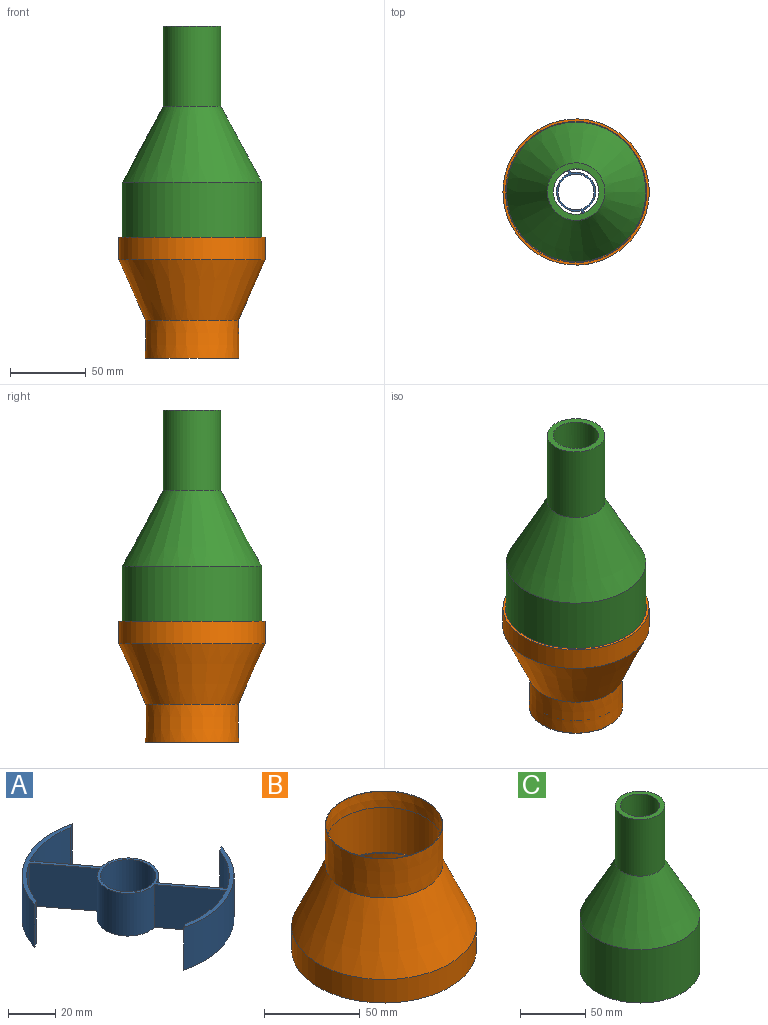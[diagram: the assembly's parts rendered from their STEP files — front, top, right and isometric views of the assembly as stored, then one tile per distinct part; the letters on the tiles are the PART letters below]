
ASSEMBLY  parts=3 mates=2
PART A: 19 faces, bbox 85.6x89.4x22 mm
  f0: cylinder r=12.95mm len=24.99mm, axis (0,0,-1), area 859.8mm2, adj f7,f10,f11,f12
  f1: plane 24.29x22mm, normal (0.8,0.6,0), area 670mm2, adj f2,f8,f10,f11
  f2: cylinder r=42.7mm len=29.3mm, axis (0,0,-1), area 668.5mm2, adj f1,f3,f10,f11
  f3: plane 22x2.6mm, normal (0.5,-0.87,0), area 66mm2, adj f2,f4,f10,f11
  f4: cylinder r=44.7mm len=53.09mm, axis (0,0,-1), area 1486.1mm2, adj f3,f5,f10,f11
  f5: plane 22x2.6mm, normal (0.5,-0.87,0), area 66mm2, adj f4,f6,f10,f11
  f6: cylinder r=42.7mm len=22mm, axis (0,0,-1), area 619.9mm2, adj f5,f7,f10,f11
  f7: plane 23.95x22mm, normal (-0.8,-0.61,0), area 661.9mm2, adj f0,f6,f10,f11
  f8: cylinder r=12.95mm len=24.99mm, axis (0,0,-1), area 859.8mm2, adj f1,f10,f11,f18
  f9: cylinder r=11.75mm len=23.5mm, axis (0,0,-1), area 1624.2mm2, adj f10,f11
  f10: plane 89.4x85.63mm, normal (0,0,1), area 442.5mm2, adj f0,f1,f2,f3,f4,f5,f6,f7
  f11: plane 89.4x85.63mm, normal (0,0,-1), area 442.5mm2, adj f0,f1,f2,f3,f4,f5,f6,f7
  f12: plane 24.29x22mm, normal (-0.8,-0.6,0), area 670mm2, adj f0,f10,f11,f13
  f13: cylinder r=42.7mm len=29.3mm, axis (0,0,-1), area 668.5mm2, adj f10,f11,f12,f14
  f14: plane 22x2.6mm, normal (-0.5,0.87,0), area 66mm2, adj f10,f11,f13,f15
  f15: cylinder r=44.7mm len=53.09mm, axis (0,0,-1), area 1486.1mm2, adj f10,f11,f14,f16
  f16: plane 22x2.6mm, normal (-0.5,0.87,0), area 66mm2, adj f10,f11,f15,f17
  f17: cylinder r=42.7mm len=22mm, axis (0,0,-1), area 619.9mm2, adj f10,f11,f16,f18
  f18: plane 23.95x22mm, normal (0.8,0.61,0), area 661.9mm2, adj f8,f10,f11,f17
PART B: 10 faces, bbox 96.4x96.4x79.7 mm
  f0: cylinder r=48.2mm len=96.4mm, axis (0,0,-1), area 4542.7mm2, adj f1,f6
  f1: plane 96.4x96.4mm, normal (0,0,-1), area 505.8mm2, adj f0,f7
  f2: plane 61.5x61.5mm, normal (0,0,1), area 43.5mm2, adj f3,f5
  f3: cone r=30.6mm half-angle=0.3deg, axis (0,0,1), area 4818.5mm2, adj f2,f6
  f4: cylinder r=30mm len=60mm, axis (0,0,1), area 5391mm2, adj f5,f8
  f5: cone r=30mm half-angle=3deg, axis (0,0,1), area 1904mm2, adj f2,f4
  f6: cone r=48.2mm half-angle=23.9deg, axis (0,0,-1), area 10750.5mm2, adj f0,f3
  f7: cylinder r=46.5mm len=93mm, axis (0,0,-1), area 4043.1mm2, adj f1,f9
  f8: cone r=0mm half-angle=59deg, axis (0,0,1), area 85mm2, adj f4,f9
  f9: cone r=46.74mm half-angle=32deg, axis (0,0,-1), area 7620.6mm2, adj f7,f8
PART C: 8 faces, bbox 92x92x153 mm
  f0: cylinder r=44.8mm len=89.6mm, axis (0,0,-1), area 14130.6mm2, adj f2,f5
  f1: cylinder r=46mm len=92mm, axis (0,0,-1), area 14451.3mm2, adj f2,f3
  f2: plane 92x92mm, normal (0,0,-1), area 342.3mm2, adj f0,f1
  f3: cone r=46mm half-angle=28.4deg, axis (0,0,-1), area 11603.7mm2, adj f1,f6
  f4: cylinder r=15mm len=73mm, axis (0,0,1), area 6880.1mm2, adj f5,f7
  f5: cone r=15mm half-angle=45deg, axis (0,0,-1), area 7917.4mm2, adj f0,f4
  f6: cylinder r=19mm len=53mm, axis (0,0,-1), area 6327.2mm2, adj f3,f7
  f7: plane 38x38mm, normal (0,0,1), area 427.3mm2, adj f4,f6
PLACE A t=(-100.92,8.61,37.59)mm
PLACE B rot(axis=(0,1,0),180deg) t=(-100.92,8.61,37.42)mm
PLACE C t=(-100.92,8.61,23.59)mm
MATE fastened B.f4 <-> C.f0  axis (0,0,1) through (-100.92,8.61,23.59)mm
MATE revolute A.f15 <-> C.f1  axis (0,0,-1) through (-100.92,8.61,48.59)mm
